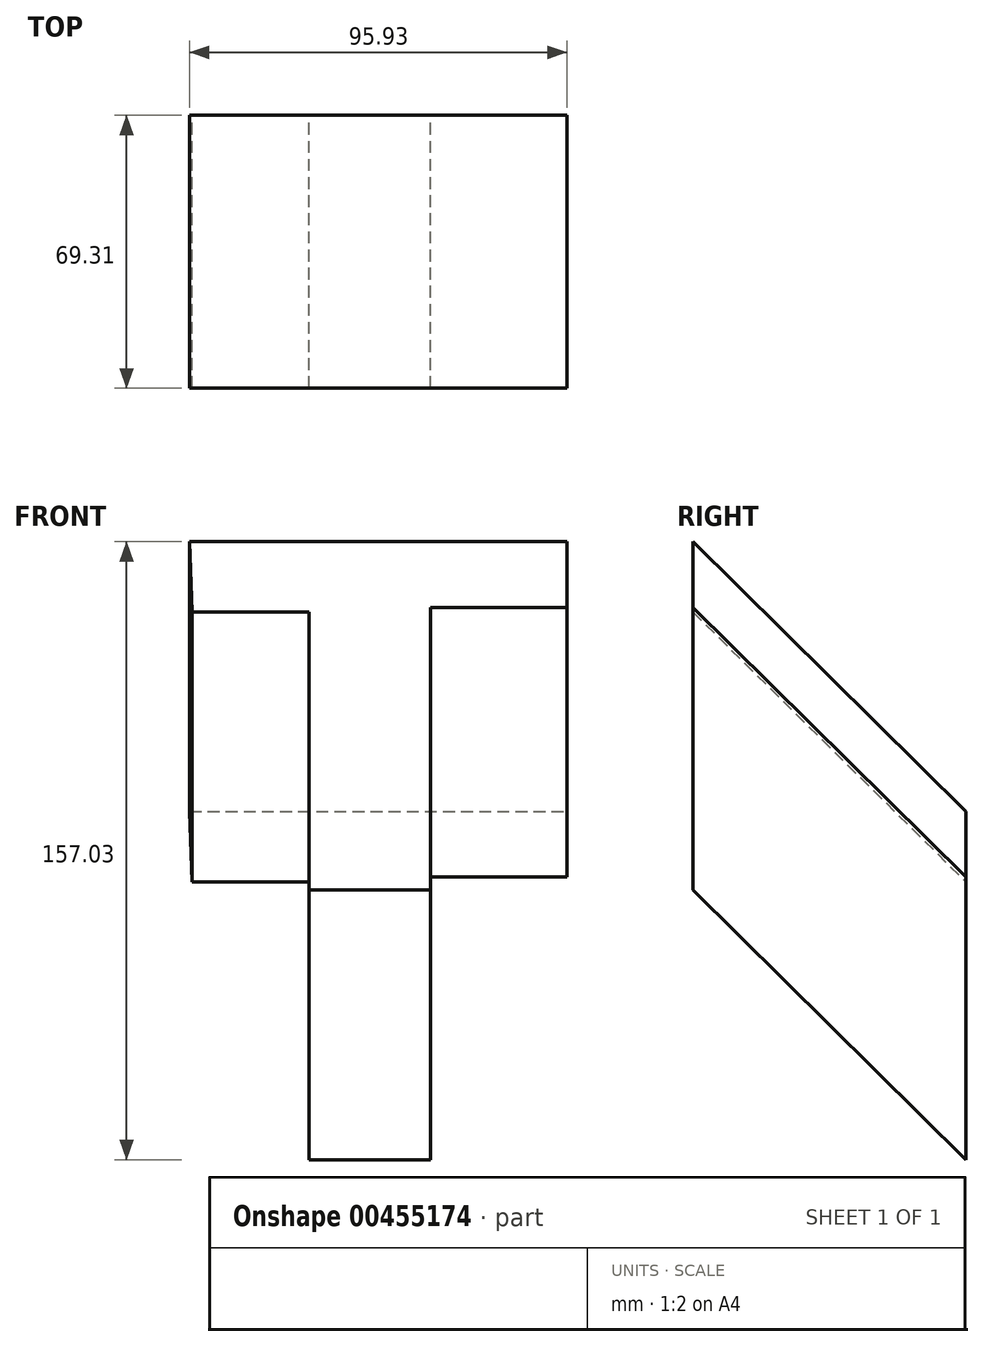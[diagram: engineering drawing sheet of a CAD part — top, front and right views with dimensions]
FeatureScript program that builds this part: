
annotation { "Feature Type Name" : "Feature", "Feature Type Description" : "" }
export const myFeature = defineFeature(function(context is Context, id is Id, definition is map)
    precondition{}
    {
        {
            var Q0;
            Q0=qCreatedBy(makeId("Front.planeOp"),FACE);
            var sketch = newSketch(context, id + "F0", { "sketchPlane" : qUnion([Q0])});
            skLineSegment(sketch, "E0", {"start": v(-44.56, 43.47) * mm, "end": v(51.37, 43.47) * mm});
            skLineSegment(sketch, "E1", {"start": v(51.37, 43.47) * mm, "end": v(51.37, 26.77) * mm});
            skLineSegment(sketch, "E2", {"start": v(51.37, 26.77) * mm, "end": v(16.7, 26.77) * mm});
            skLineSegment(sketch, "E3", {"start": v(16.7, 26.77) * mm, "end": v(16.7, -45.02) * mm});
            skLineSegment(sketch, "E4", {"start": v(16.7, -45.02) * mm, "end": v(-14.23, -45.02) * mm});
            skLineSegment(sketch, "E5", {"start": v(-14.23, -45.02) * mm, "end": v(-14.23, 25.53) * mm});
            skLineSegment(sketch, "E6", {"start": v(-14.23, 25.53) * mm, "end": v(-43.94, 25.53) * mm});
            skLineSegment(sketch, "E7", {"start": v(-43.94, 25.53) * mm, "end": v(-44.56, 43.47) * mm});
            skSolve(sketch);
        }
        {
            var Q0;
            Q0=qCreatedBy(makeId("Right.planeOp"),FACE);
            var sketch = newSketch(context, id + "F1", { "sketchPlane" : qUnion([Q0])});
            skLineSegment(sketch, "E8", {"start": v(0, 0) * mm, "end": v(69.31, -68.54) * mm});
            skSolve(sketch);
        }
        {
            var Q0;
            Q0 = qSketchRegion(id + "F0", true);
            var Q1;
            Q1=sQuery(id+"F1.wireOp",EDGE,"E8");
            sweep(context, id + "F2", {"profiles" : qUnion([Q0]), "path" : qUnion([Q1])});
        }
    });
